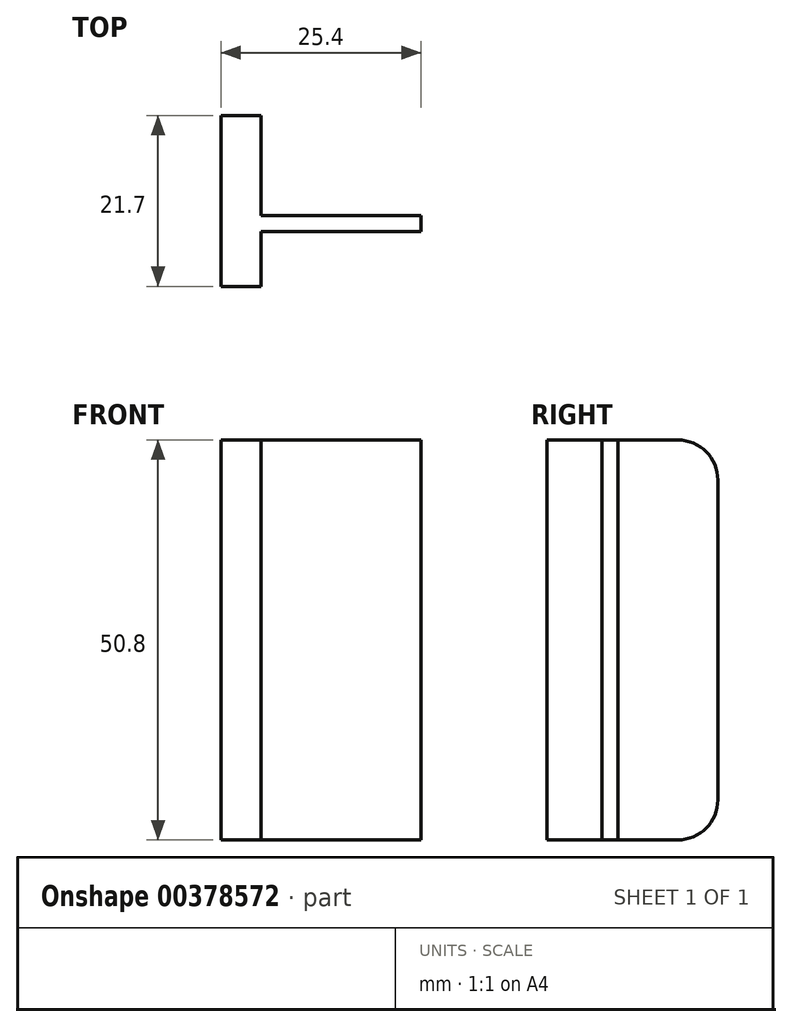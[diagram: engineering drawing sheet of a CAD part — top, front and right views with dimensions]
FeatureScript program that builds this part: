
annotation { "Feature Type Name" : "Feature", "Feature Type Description" : "" }
export const myFeature = defineFeature(function(context is Context, id is Id, definition is map)
    precondition{}
    {
        {
            var Q0;
            Q0=qCreatedBy(makeId("Front.planeOp"),FACE);
            var sketch = newSketch(context, id + "F0", { "sketchPlane" : qUnion([Q0])});
            skLineSegment(sketch, "E0", {"start": v(0, 0) * mm, "end": v(0, 50.8) * mm});
            skLineSegment(sketch, "E1", {"start": v(0, 50.8) * mm, "end": v(25.4, 50.8) * mm});
            skLineSegment(sketch, "E2", {"start": v(25.4, 50.8) * mm, "end": v(25.4, 0) * mm});
            skLineSegment(sketch, "E3", {"start": v(0, 0) * mm, "end": v(25.4, 0) * mm});
            skSolve(sketch);
        }
        {
            var Q0;
            Q0=makeQuery(id+"F0.imprint","IMPRINT",FACE,{"disambiguationData":[TD([[makeQuery(id+"F0.imprint","IMPRINT",EDGE,{"derivedFrom":sQuery(id+"F0.wireOp",EDGE,"E0")}),-1.0]])]});
            extrude(context, id + "F1", {"entities" : qUnion([Q0]), "depth" : 2 * mm});
        }
        {
            var Q0;
            Q0=makeQuery(id+"F1.opExtrude","CAP_FACE",FACE,{"disambiguationData":[OSD([sQuery(id+"F0.wireOp",EDGE,"E0"),sQuery(id+"F0.wireOp",EDGE,"E1"),sQuery(id+"F0.wireOp",EDGE,"E2"),sQuery(id+"F0.wireOp",EDGE,"E3")])],"isStart":false});
            var sketch = newSketch(context, id + "F2", { "sketchPlane" : qUnion([Q0])});
            skLineSegment(sketch, "E4", {"start": v(0, 50.8) * mm, "end": v(5.08, 50.8) * mm});
            skLineSegment(sketch, "E5", {"start": v(5.08, 50.8) * mm, "end": v(5.08, 0) * mm});
            skLineSegment(sketch, "E6", {"start": v(5.08, 0) * mm, "end": v(0, 0) * mm});
            skLineSegment(sketch, "E7", {"start": v(0, 0) * mm, "end": v(0, 50.8) * mm});
            skSolve(sketch);
        }
        {
            var Q0;
            Q0 = qSketchRegion(id + "F2", true);
            extrude(context, id + "F3", {"entities" : qUnion([Q0]), "operationType" : NewBodyOperationType.ADD, "depth" : 7 * mm});
        }
        {
            var Q0;
            Q0=makeQuery(id+"F1.opExtrude","CAP_FACE",FACE,{"disambiguationData":[OSD([sQuery(id+"F0.wireOp",EDGE,"E0"),sQuery(id+"F0.wireOp",EDGE,"E1"),sQuery(id+"F0.wireOp",EDGE,"E2"),sQuery(id+"F0.wireOp",EDGE,"E3")])],"isStart":true});
            var sketch = newSketch(context, id + "F4", { "sketchPlane" : qUnion([Q0])});
            skLineSegment(sketch, "E8", {"start": v(0, 50.8) * mm, "end": v(0, 0) * mm});
            skLineSegment(sketch, "E9", {"start": v(0, 0) * mm, "end": v(-5.08, 0) * mm});
            skLineSegment(sketch, "E10", {"start": v(-5.08, 0) * mm, "end": v(-5.08, 50.8) * mm});
            skLineSegment(sketch, "E11", {"start": v(-5.08, 50.8) * mm, "end": v(0, 50.8) * mm});
            skSolve(sketch);
        }
        {
            var Q0;
            Q0 = qSketchRegion(id + "F4", true);
            extrude(context, id + "F5", {"entities" : qUnion([Q0]), "operationType" : NewBodyOperationType.ADD, "depth" : 12.7 * mm});
        }
        {
            var Q0;
            Q0=makeQuery(id+"F5.opExtrude","CAP_EDGE",EDGE,{"disambiguationData":[OSD([sQuery(id+"F4.wireOp",EDGE,"E11")])],"isStart":false});
            var Q1;
            Q1=makeQuery(id+"F5.opExtrude","CAP_EDGE",EDGE,{"disambiguationData":[OSD([sQuery(id+"F4.wireOp",EDGE,"E9")])],"isStart":false});
            fillet(context, id + "F6", {"entities" : qUnion([Q0, Q1]), "radius" : 5.08 * mm, "tangentPropagation" : true, "allowEdgeOverflow" : false});
        }
    });
